# Revit family: Legrand Coffret Plexo³ 4-8 modules
name_source: partatom
category: Equipement électrique
revit_build: Autodesk Revit 2018 (Build: 20170223_1515(x64)
units: mm (PartAtom-declared; Revit-internal decimal feet)

## family parameters
Basée sur le plan de construction = Non
Configuration du panneau = Deux colonnes, circuits au sein
Cote de connecteur circulaire = Utiliser le diamètre
Couper avec des vides une fois chargée = Non
Numéro OmniClass = 23.80.30.11.17
Partagée = Non
Point de calcul de pièce = Non
Titre OmniClass = Distribution Boards and Control Panels
Toujours verticalement = Oui
Type d'élément = Tableau de raccordement

## types (13) — shared parameters
Conditions Générale d'Utilisation = https://export.legrand.com
ETIM Class 6.0 = EC000214
Fabricant = Legrand
IK = 09
IP = 65
Matière = Polystyrène
RAL = 7046
URL = www.legrand.fr

## per-type parameters (varying)
| type | Bornier N | Bornier T | Coffret 001904 | Coffret 001906 | Coffret 001908 | Coffret 601954 | Coffret 601956 | Coffret 601958 | Coffret 601974 | Coffret 601976 | Coffret 601978 | Coffret 601994 | Coffret 601996 | Coffret 601998 | Description | Image du type |
| Plexo³ 4 modules 1 rangée  001904 |  |  | Oui | Non | Non | Non | Non | Non | Non | Non | Non | Non | Non | Non | Plexo³ 4 modules 1 rangée  001904 | plexo3_6modules_001906_pw_182611_pz_4.jpg |
| Plexo³ 6 modules 1 rangée  001906 |  | Bornier 1+6 trous | Non | Oui | Non | Non | Non | Non | Non | Non | Non | Non | Non | Non | Plexo³ 6 modules 1 rangée  001906 | plexo3_6modules_001906_pw_182611_pz_4.jpg |
| Plexo³ 8 modules 1 rangée  001908 |  | Bornier 1+6 trous | Non | Non | Oui | Non | Non | Non | Non | Non | Non | Non | Non | Non | Plexo³ 8 modules 1 rangée  001908 | <Aucun> |
| Plexo³ 4 modules 1 rangée  601954 |  |  | Non | Non | Non | Oui | Non | Non | Non | Non | Non | Non | Non | Non | Plexo³ 4 modules 1 rangée  601954 | plexo3_6modules_001906_pw_182611_pz_4.jpg |
| Plexo³ 4 modules 1 rangée  601974 | Bornier 4 trous | Bornier 4 trous | Non | Non | Non | Non | Non | Non | Oui | Non | Non | Non | Non | Non | Plexo³ 4 modules 1 rangée  601974 | plexo3_6modules_001906_pw_182611_pz_4.jpg |
| Plexo³ 4 modules 1 rangée  601996 |  |  | Non | Non | Non | Non | Non | Non | Non | Non | Non | Non | Oui | Non | Plexo³ 4 modules 1 rangée  601996 | plexo3_6modules_001906_pw_182611_pz_4.jpg |
| Plexo³ 6 modules 1 rangée  601956 |  |  | Non | Non | Non | Non | Oui | Non | Non | Non | Non | Non | Non | Non | Plexo³ 6 modules 1 rangée  601956 | plexo3_6modules_001906_pw_182611_pz_4.jpg |
| Plexo³ 6 modules 1 rangée  601976 | Bornier 4 trous | Bornier 4 trous | Non | Non | Non | Non | Non | Non | Non | Oui | Non | Non | Non | Non | Plexo³ 6 modules 1 rangée  601976 | plexo3_6modules_001906_pw_182611_pz_4.jpg |
| Plexo³ 8 modules 1 rangée  601958 |  |  | Non | Non | Non | Non | Non | Oui | Non | Non | Non | Non | Non | Non | Plexo³ 8 modules 1 rangée  601958 | <Aucun> |
| Plexo³ 8 modules 1 rangée  601978 | Bornier 8 trous | Bornier 8 trous | Non | Non | Non | Non | Non | Non | Non | Non | Oui | Non | Non | Non | Plexo³ 8 modules 1 rangée  601978 | <Aucun> |
| Plexo³ 8 modules 1 rangée  601998 | Bornier 8 trous | Bornier 8 trous | Non | Non | Non | Non | Non | Non | Non | Non | Non | Non | Non | Oui | Plexo³ 8 modules 1 rangée  601978 | <Aucun> |
| Plexo³ 8 modules 1 rangée  601996 | Bornier 8 trous | Bornier 8 trous | Non | Non | Non | Non | Non | Non | Non | Non | Non | Non | Oui | Non | Plexo³ 6 modules 1 rangée  601996 | <Aucun> |
| Plexo³ 8 modules 1 rangée  601994 | Bornier 8 trous | Bornier 8 trous | Non | Non | Non | Non | Non | Non | Non | Non | Non | Oui | Non | Non | Plexo³ 4 modules 1 rangée  601994 | <Aucun> |
